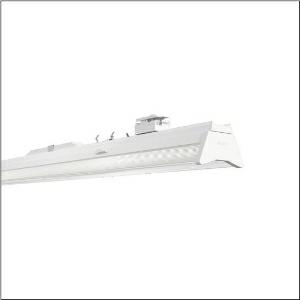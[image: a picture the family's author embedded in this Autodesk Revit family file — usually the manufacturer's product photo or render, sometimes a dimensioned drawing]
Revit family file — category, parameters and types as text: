
# Revit family: licross_21_performance_mo_52tm16dn46xg
name_source: partatom
category: Lighting Fixtures
units: mm (PartAtom-declared; Revit-internal decimal feet)

## family parameters
Cut with Voids When Loaded = No
Host = Face
Light Source = No
Part Type = Normal
Room Calculation Point = No
Round Connector Dimension = Use Diameter
Shared = No

## types (1)
- --- (1 x LED, 6000 lm, 32.7 W, 4000K)
    Apparent Load = 33 VA
    CIE Flux Codes = 66 88 96 79 100
    Color Rendering = 80
    Color Temperature = 4000K
    Default Elevation = 1800 mm
    Description = Licross 21 Performance MO, luminaire insert, of sheet steel, galvanised, coil coated, white, length: 1.500mm, width: 120mm, height: 123mm, LED rated luminous flux: 6.000lm, light colour: 840, SDCM (Standard Deviation of Colour Matching)MacAdam ≤ 3 SDCM (initial), control gear: DALI 2, with plug, 5-pole, with phase selection, mains connection: 220..240V, AC, 50/60Hz, rated input power: 33W, internal wiring halogen-free, primary light control with lens, of plastic, primary optical cover: cover, of PMMA, light emission: direct/indirect distribution, primary light characteristic: symmetric, protection rating (complete): IP40, insulation class (complete): insulation class I (protective earthing), certification: CE, ENEC, UKCA, protection symbol: D if used in an environment without relevant dust loads with corresponding accessories, impact resistance: IK06, permissible ambient temperature for indoor applications: -25..+45°C, corresponds to IFS (International Featured Standards) requirements for safety and quality in the food industry, reducing of maximum allowable ambient temperature of 5°C with ceiling mounting, LABS conformity tested according to VDMA 24364:2018-05, The light source and the operating device comply with the requirements of the Ecodesign Regulation (EU) 2019/2020 and are replaceable in accordance with this regulation, packaging unit: 1 piece
    Height = 114 mm
    Lamp = 1 x LED
    Lamp Light Flux = 6000 lm
    Lamp Power = 32.7 W
    Lamp count = 1
    Length = 1500 mm
    Luminous efficacy = 183 lm/W
    Manufacturer = Siteco
    ModVariant = No
    Model = 52TM16DN46XG
    Mounting Place = Ceiling
    Mounting Type = Pendant
    Number of Poles = 1
    OnlyDefault = Yes
    Power Factor = 1
    Product Name = Licross 21 Performance MO
    Product group = luminaire insert | ceiling pendant
    ProductGroupID = 901
    Protection Class = Protection class I
    Protection Degree = IP 40
    RLX_Detail_Level = 1
    RLX_Emergency_Light_Flux = 0 lm
    RLX_Emergency_Type = 0
    RLX_Emergency_Type_DB = No
    RlxData = <blob elided: 34005 chars, md5=6f636c6f>
    Socket = socket
    Standby Power = 0 W
    System Light Flux = 6000 lm
    System Power = 33 W
    Type Comments = factory setting: luminous flux: 100 % | dim-lin: 254 | 222 mA
    Type Image = l_1256138.jpg
    URL = http://relux.com
    VarID = @adj_129435
    Voltage = 0 V
    Weight = 0.00 kg
    Width = 120 mm

## geometry (parser evidence)
native form markers: Blend x4, Sweep x12
no freeform markers — native parametric forms only
